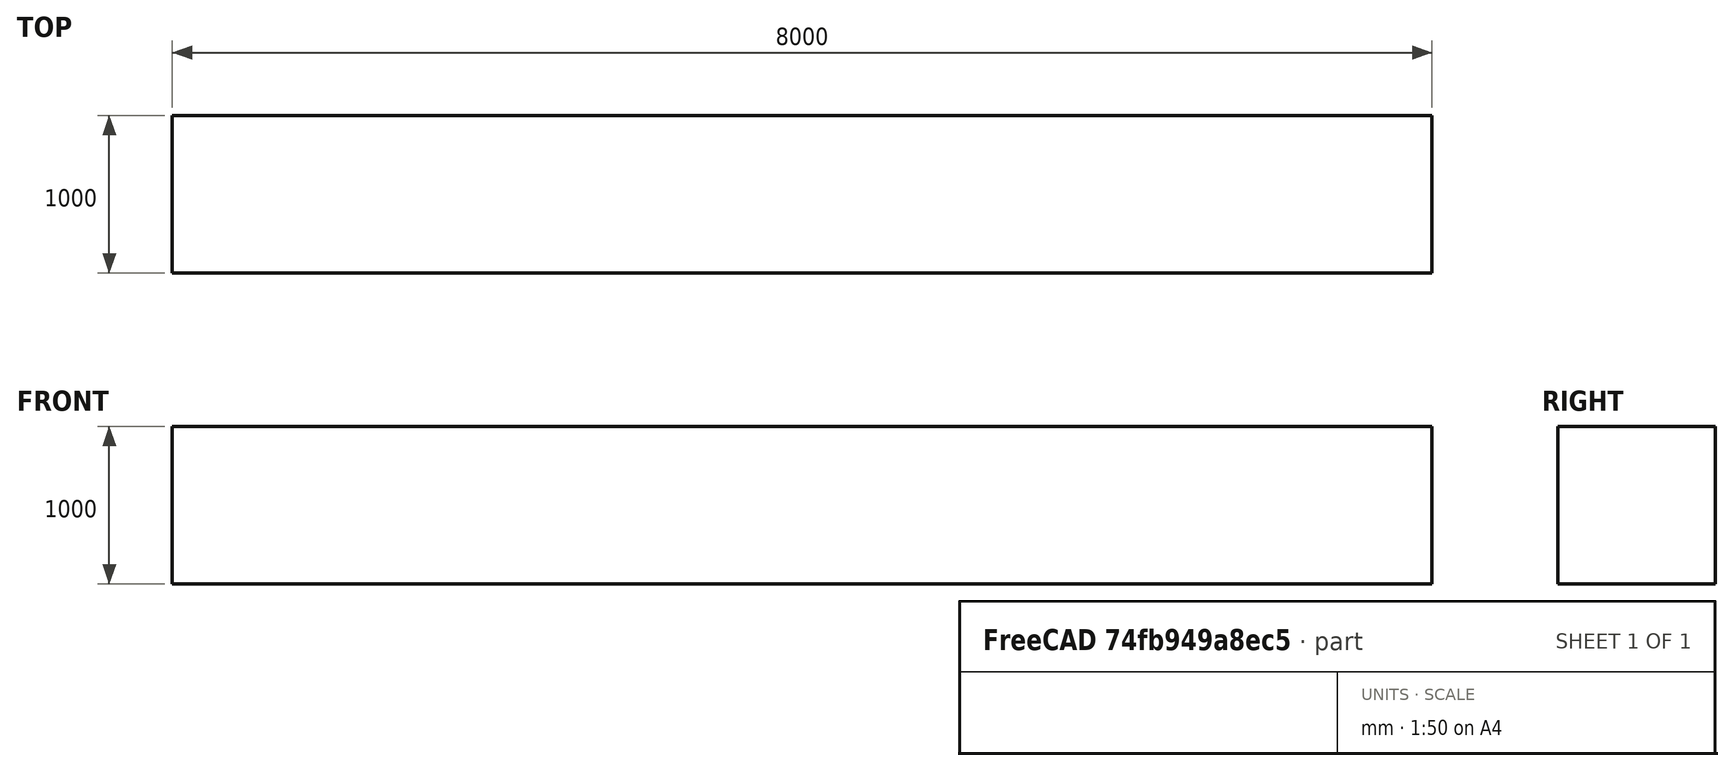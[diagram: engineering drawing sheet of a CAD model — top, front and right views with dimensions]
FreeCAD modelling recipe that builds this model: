
FCSTD DOCUMENT  (FreeCAD 0.21R33668 +26 (Git))
Label: FEM-essai1
License: All rights reserved
LicenseURL: http://en.wikipedia.org/wiki/All_rights_reserved
objects: Part::Box×1, Fem::ConstraintFixed×1, Fem::ConstraintForce×1, App::MaterialObjectPython×1, Fem::FemMeshShapeNetgenObject×1, Fem::FemSolverObjectPython×1, Fem::FemPostPipeline×1, Fem::FemMeshObjectPython×1, Fem::FemResultObjectPython×1, Fem::FemAnalysis×1
note: 1 computed .brp shape members not serialized (recipe doc carries the construction recipe); baked Part::Feature solids carry a one-line shape summary decoded from their .brp

FEATURE [Part::Box] Box  label="Cube"
  AttacherType = Attacher::AttachEngine3D
  Height = 1000
  Length = 8000
  Width = 1000
  expr: Length = 8 m
FEATURE [Fem::ConstraintFixed] ConstraintFixed
  NormalDirection = (-1,0,0)
  Normals = (16) [(-1,0,0),(-1,0,0),(-1,0,0),(-1,0,0),(-1,0,0),(-1,0,0),(-1,0,0),(-1,0,0),(-1,0,0),(-1,0,0),(-1,0,0),(-1,0,0),(-1,0,0),(-1,0,0),(-1,0,0),(-1,0,0)]
  Points = (16) [(0,1000,0),(0,1000,333.333),(0,1000,666.667),(0,1000,1000),(0,666.667,0),(0,666.667,333.333),(0,666.667,666.667),(0,666.667,1000),(0,333.333,0),+7 more]
  References = -> [Box]
  Scale = 33
FEATURE [Fem::ConstraintForce] ConstraintForce
  Direction = -> Box [Edge1]
  DirectionVector = (0,0,1)
  Force = 9000000
  NormalDirection = (1,0,0)
  Points = (16) [(8000,1000,0),(8000,1000,333.333),(8000,1000,666.667),(8000,1000,1000),(8000,666.667,0),(8000,666.667,333.333),(8000,666.667,666.667),+9 more]
  References = -> [Box]
  Scale = 33
FEATURE [App::MaterialObjectPython] MaterialSolid  # material (typed FeaturePython)
  Category = 0
  Material = AuthorAndLicense=(c) 2013 Juergen Riegel (CC-BY 3.0),CardName=CalculiX-Steel,Density=7900 kg/m^3,+8 more (map truncated)
FEATURE [Fem::FemMeshShapeNetgenObject] FEMMeshNetgen
  Fineness = 4
  GrowthRate = 0.3
  MaxSize = 1000
  NbSegsPerEdge = 1
  NbSegsPerRadius = 2
  Optimize = true
  SecondOrder = true
  Shape = -> Box
FEATURE [Fem::FemSolverObjectPython] SolverCalculix  # FEM object (typed FeaturePython)
  AnalysisType = 0
  BeamShellResultOutput3D = false
  BucklingFactors = 1
  EigenmodeHighLimit = 1000000
  EigenmodeLowLimit = 0
  EigenmodesCount = 10
  GeometricalNonlinearity = 0
  IterationsControlParameterCutb = 0.25,0.5,0.75,0.85,,,1.5,
  IterationsControlParameterIter = 4,8,9,200,10,400,,200,,
  IterationsControlParameterTimeUse = false
  IterationsThermoMechMaximum = 200
  IterationsUserDefinedIncrementations = false
  IterationsUserDefinedTimeStepLength = false
  MaterialNonlinearity = 0
  MatrixSolverType = 0
  SplitInputWriter = false
  ThermoMechSteadyState = true
  TimeEnd = 1
  TimeInitialStep = 1
FEATURE [Fem::FemPostPipeline] Pipeline_CalculiX_static_Results
  Mode = 2
FEATURE [Fem::FemMeshObjectPython] CalculiX_static_Results_Mesh  # FEM object (typed FeaturePython)
FEATURE [Fem::FemResultObjectPython] CalculiX_static_Results  # FEM object (typed FeaturePython)
  DisplacementLengths = [88.1098,88.1095,88.0989,88.0995,0,0,0,0,0,0,0.757386,1.76447,3.65385,7.02421,11.8773,18.6145,27.8142,36.7739,45.5455,53.8909,61.7979,69.1648,75.9456,82.297,88.1065,88.1089,0.763475,1.74353,3.29167,5.59366,8.87864,13.3765,19.252,26.9765,+720 more]
  DisplacementVectors = (754) [(8.17529,-0.00297488,87.7297),(-8.17429,-0.00888355,87.7295),(8.17444,0.000832699,87.7188),(-8.17539,-0.013553,87.7194),(0,0,0),(0,0,0),(0,0,0),+747 more]
  Eigenmode = 0
  EigenmodeFrequency = 0
  MaxShear = [5.62828,5.76282,5.09254,5.72419,194.648,198.552,193.993,194.863,152.387,163.573,212.928,193.017,182.673,165.772,149.978,131.738,106.372,87.8806,75.202,58.4946,44.394,31.8919,20.6939,9.80654,5.88231,4.70766,223.156,193.262,185.839,173.467,+724 more]
  Mesh = -> CalculiX_static_Results_Mesh
  NodeNumbers = [1,2,3,4,5,6,7,8,9,10,11,12,13,14,15,16,17,18,19,20,21,22,23,24,25,26,27,28,29,30,31,32,33,34,35,36,37,38,39,40,41,42,43,44,45,46,47,48,49,50,51,52,53,54,55,56,57,58,59,60,61,62,63,64,65,66,67,68,69,+685 more]
  NodeStrainXX = [2.3503e-05,-2.37238e-05,2.3134e-05,-2.32878e-05,0.00190145,-0.00190374,0.00188518,-0.00187639,-0.00159414,-0.00167823,-0.00194254,-0.00183666,-0.00173831,-0.00157717,-0.00142656,-0.00125105,-0.00100759,-0.000832686,-0.000710028,-0.00055368,+734 more]
  NodeStrainXY = [1.83924e-06,-3.00345e-06,-1.54993e-06,3.2483e-06,-0.000672291,0.000696088,0.00067074,-0.000689243,-0.000216129,0.000179736,3.21916e-05,-7.22661e-06,-6.60408e-06,-7.87091e-06,-9.09984e-06,-1.08432e-05,-1.15458e-05,-3.66748e-06,-6.06871e-06,+735 more]
  NodeStrainXZ = [2.37979e-05,2.50821e-05,2.02857e-05,2.55942e-05,0.000309987,0.000346662,0.00032221,0.000316047,0.000455908,0.000307592,-7.86966e-05,6.10869e-06,2.58994e-05,2.51303e-05,2.74802e-05,3.19796e-05,5.46399e-05,6.22745e-05,5.93078e-05,2.88909e-05,+734 more]
  NodeStrainYY = [2.15474e-06,-7.89556e-07,2.03057e-06,-1.14652e-06,2.71852e-09,-2.57627e-09,2.45566e-09,-2.51723e-09,4.26003e-05,4.19294e-05,0.000607308,0.000552654,0.000520602,0.000470687,0.000427799,0.000370773,0.000295821,0.00025139,0.000213673,+735 more]
  NodeStrainYZ = [3.06838e-06,2.30627e-06,-3.9409e-06,-4.21394e-06,-3.26321e-10,-6.16197e-10,7.02405e-10,5.25964e-10,1.88039e-05,-2.75643e-05,8.68167e-06,1.28429e-06,-2.83338e-07,-9.98192e-07,-8.6343e-07,3.44091e-06,1.75975e-07,-4.4032e-07,2.49461e-07,+735 more]
  NodeStrainZZ = [-2.68674e-05,2.64174e-05,-2.4382e-05,2.45303e-05,2.95465e-09,-2.82562e-09,2.92377e-09,-2.83092e-09,8.25132e-06,0.000231835,0.000687892,0.000548467,0.000522689,0.000474317,0.000428959,0.000377429,0.000304748,0.000247026,0.000213414,+735 more]
  NodeStressXX = [3.65009,-3.60163,3.83184,-3.75024,537.525,-538.173,532.925,-530.441,-444.49,-441.255,-392.221,-385.805,-365.007,-331.362,-299.478,-263.015,-212.077,-175.009,-148.976,-116.437,-88.3732,-63.3221,-40.7864,-19.7061,-3.79008,-2.86411,-402.421,+727 more]
  NodeStressXY = [0.297108,-0.485172,-0.250374,0.524726,-108.601,112.445,108.35,-111.339,-34.9131,29.0342,5.20018,-1.16737,-1.06681,-1.27146,-1.46997,-1.75159,-1.8651,-0.592438,-0.98033,-1.58398,-1.11216,-0.979837,-0.919812,-0.536245,0.505595,-0.752055,+728 more]
  NodeStressXZ = [3.84427,4.05172,3.27693,4.13445,50.0748,55.9992,52.0494,51.0538,73.6467,49.688,-12.7125,0.986789,4.18374,4.0595,4.43911,5.16593,8.82644,10.0597,9.5805,4.667,3.69378,3.82159,3.58032,1.70491,3.3423,2.75913,-7.52237,0.584043,3.517,4.47113,+724 more]
  NodeStressYY = [0.201521,0.103137,0.422826,-0.173572,230.369,-230.646,228.397,-227.332,-180.094,-163.383,19.6763,0.1616,-0.106525,-0.554821,0.0720627,-1.02801,-1.52597,0.11104,0.236919,0.124092,0.0618425,0.0355177,0.0327227,-0.351114,2.18103,1.5607,21.803,+727 more]
  NodeStressYZ = [0.495661,0.372552,-0.636607,-0.680714,-5.27135e-05,-9.95395e-05,0.000113465,8.49634e-05,3.03755,-4.4527,1.40242,0.207462,-0.04577,-0.161246,-0.139477,0.555839,0.0284267,-0.0711286,0.0402976,0.467119,-0.0529635,-0.00230914,-0.0444716,+731 more]
  NodeStressZZ = [-4.48667,4.49811,-3.84382,3.97423,230.369,-230.646,228.397,-227.333,-185.642,-132.706,32.6938,-0.514866,0.230657,0.0316446,0.259454,0.0472053,-0.0839319,-0.593817,0.195046,-0.672224,0.0352965,-0.0355899,-0.116268,-2.34446,5.83938,4.63201,+728 more]
  PrincipalMax = [5.22115,6.18108,5.0852,5.79891,578.595,-185.857,574.654,-184.024,-163.345,-124.901,33.1893,0.222062,0.287183,0.127508,0.404982,0.347874,0.284268,0.171855,0.80872,0.342474,0.246907,0.216829,0.268291,-0.275575,6.88621,5.54554,43.6944,+727 more]
  PrincipalMed = [0.179199,0.163089,0.425524,-0.0990178,230.369,-230.646,228.397,-227.333,-178.764,-160.394,19.6274,-0.569267,-0.112018,-0.596093,-0.000546242,-1.21542,-1.51083,-0.0743748,0.242456,-0.680799,0.0181729,0.0280688,-0.0188232,-2.23745,2.22253,+729 more]
  PrincipalMin = [-6.03541,-5.34455,-5.09988,-5.64947,189.299,-582.962,186.668,-573.75,-468.118,-452.048,-392.668,-385.811,-365.058,-331.417,-299.551,-263.128,-212.46,-175.589,-149.595,-116.647,-88.5411,-63.5671,-41.1194,-19.8887,-4.87841,-3.86977,-402.617,+727 more]
  ResultType = Fem::ResultMechanical
  Stats = [-8.17903,8.17949,-0.276822,0.278409,0,87.7306,0,88.1111,7.42575,435.517,-190.946,578.595,-230.646,230.369,-582.962,189.299,4.24879,223.156,0,0,0,0,0,0,0,0]
  Time = 0
  vonMises = [9.76608,9.98475,8.83116,9.91611,370.472,376.712,368.896,369.978,297.364,310.923,419.24,385.638,365.146,331.183,299.753,262.698,211.853,175.638,150.122,116.481,88.6739,63.6897,41.2449,18.7094,10.2611,8.19453,435.517,386.462,371.411,346.183,+724 more]
FEATURE [Fem::FemAnalysis] Analysis
  Group = -> [ConstraintFixed,ConstraintForce,MaterialSolid,FEMMeshNetgen,SolverCalculix,Pipeline_CalculiX_static_Results,CalculiX_static_Results]
